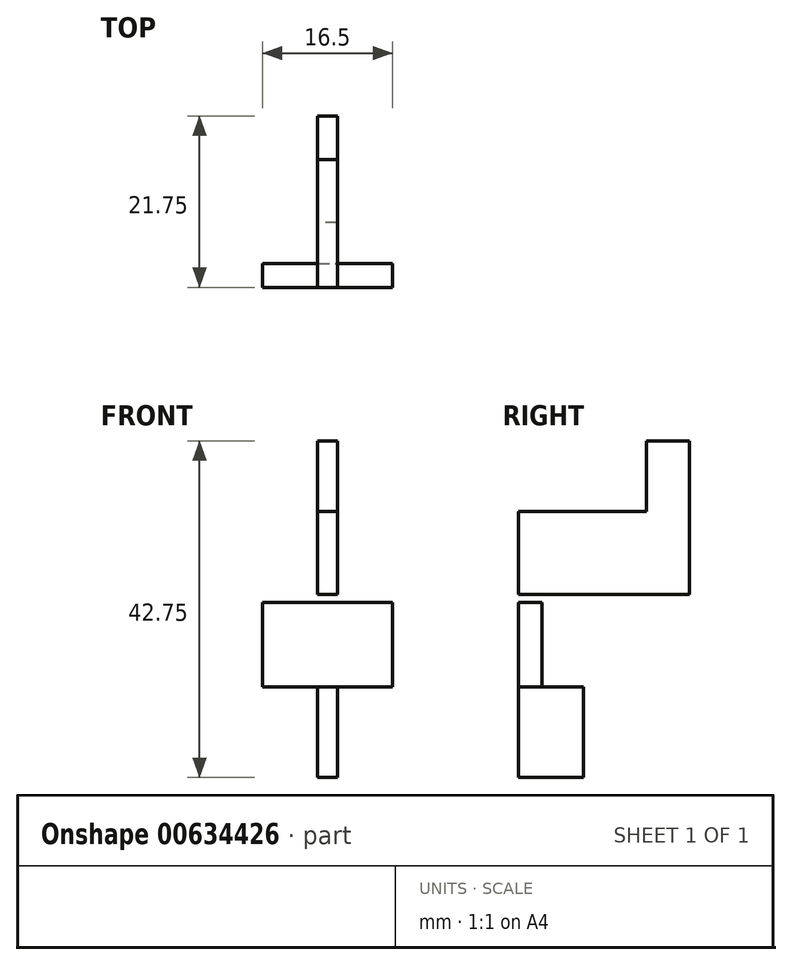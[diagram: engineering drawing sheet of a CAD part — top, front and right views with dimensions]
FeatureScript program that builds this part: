
annotation { "Feature Type Name" : "Feature", "Feature Type Description" : "" }
export const myFeature = defineFeature(function(context is Context, id is Id, definition is map)
    precondition{}
    {
        {
            var Q0;
            Q0=qCreatedBy(makeId("Right.planeOp"),FACE);
            var sketch = newSketch(context, id + "F0", { "sketchPlane" : qUnion([Q0])});
            skLineSegment(sketch, "E0.bottom", {"start": v(0, 0) * mm, "end": v(203.2, 0) * mm});
            skLineSegment(sketch, "E0.top", {"start": v(0, 5) * mm, "end": v(203.2, 5) * mm});
            skLineSegment(sketch, "E0.left", {"start": v(0, 0) * mm, "end": v(0, 5) * mm});
            skLineSegment(sketch, "E0.right", {"start": v(203.2, 0) * mm, "end": v(203.2, 5) * mm});
            skLineSegment(sketch, "E1.bottom", {"start": v(0, 0) * mm, "end": v(5, 0) * mm});
            skLineSegment(sketch, "E1.top", {"start": v(0, -95) * mm, "end": v(5, -95) * mm});
            skLineSegment(sketch, "E1.left", {"start": v(0, 0) * mm, "end": v(0, -95) * mm});
            skLineSegment(sketch, "E1.right", {"start": v(5, 0) * mm, "end": v(5, -95) * mm});
            skSolve(sketch);
        }
        {
            assignVariable(context, id + "F1", {"name" : "BracketThick", "anyValue" : 2.5 * mm});
        }
        {
            assignVariable(context, id + "F2", {"name" : "BracketNubThick", "anyValue" : 7 * mm});
        }
        {
            var Q0;
            Q0=qCreatedBy(makeId("Right.planeOp"),FACE);
            var sketch = newSketch(context, id + "F3", { "sketchPlane" : qUnion([Q0])});
            skLineSegment(sketch, "E2", {"start": v(0, -19.5) * mm, "end": v(0, -9) * mm});
            skLineSegment(sketch, "E3", {"start": v(0, -31.25) * mm, "end": v(0, -42.75) * mm});
            skLineSegment(sketch, "E4.MirrorCS", {"start": v(16.25, 0) * mm, "end": v(21.75, 0) * mm});
            skLineSegment(sketch, "E5.MirrorCS", {"start": v(8.25, -31.25) * mm, "end": v(0, -31.25) * mm});
            skLineSegment(sketch, "E6.MirrorCS", {"start": v(16.25, -9) * mm, "end": v(16.25, 0) * mm});
            skLineSegment(sketch, "E7.MirrorCS", {"start": v(0, -9) * mm, "end": v(16.25, -9) * mm});
            skLineSegment(sketch, "E8.MirrorCS", {"start": v(21.75, 0) * mm, "end": v(21.75, -19.5) * mm});
            skLineSegment(sketch, "E9.MirrorCS", {"start": v(0, -42.75) * mm, "end": v(8.25, -42.75) * mm});
            skLineSegment(sketch, "E10.MirrorCS", {"start": v(21.75, -19.5) * mm, "end": v(0, -19.5) * mm});
            skLineSegment(sketch, "E11.MirrorCS", {"start": v(8.25, -42.75) * mm, "end": v(8.25, -31.25) * mm});
            skLineSegment(sketch, "E12", {"start": v(3, -20.5) * mm, "end": v(3, -31.25) * mm});
            skLineSegment(sketch, "E13.MirrorCS", {"start": v(3, -31.25) * mm, "end": v(0, -31.25) * mm});
            skLineSegment(sketch, "E14.MirrorCS", {"start": v(0, -31.25) * mm, "end": v(0, -20.5) * mm});
            skLineSegment(sketch, "E15.MirrorCS", {"start": v(0, -20.5) * mm, "end": v(3, -20.5) * mm});
            skLineSegment(sketch, "E16.bottom", {"start": v(0, -19.5) * mm, "end": v(1, -19.5) * mm});
            skLineSegment(sketch, "E16.top", {"start": v(0, -20.5) * mm, "end": v(1, -20.5) * mm});
            skLineSegment(sketch, "E16.left", {"start": v(0, -19.5) * mm, "end": v(0, -20.5) * mm});
            skLineSegment(sketch, "E16.right", {"start": v(1, -19.5) * mm, "end": v(1, -20.5) * mm});
            skSolve(sketch);
        }
        {
            var Q0;
            Q0=makeQuery(id+"F3.imprint","IMPRINT",FACE,{"disambiguationData":[TD([[makeQuery(id+"F3.imprint","IMPRINT",EDGE,{"derivedFrom":sQuery(id+"F3.wireOp",EDGE,"E2")}),-1.0]])]});
            var Q1;
            Q1=makeQuery(id+"F3.imprint","IMPRINT",FACE,{"disambiguationData":[TD([[makeQuery(id+"F3.imprint","IMPRINT",EDGE,{"derivedFrom":sQuery(id+"F3.wireOp",EDGE,"E3")}),1.0]])]});
            extrude(context, id + "F4", {"entities" : qUnion([Q0, Q1]), "depth" : getVariable(context, 'BracketThick'), "offsetDistance" : 25 * mm});
        }
        {
            var Q0;
            Q0=makeQuery(id+"F3.imprint","IMPRINT",FACE,{"disambiguationData":[TD([[makeQuery(id+"F3.imprint","IMPRINT",EDGE,{"derivedFrom":sQuery(id+"F3.wireOp",EDGE,"E12")}),-1.0]])]});
            var Q1;
            Q1=makeQuery(id+"F3.imprint","IMPRINT",FACE,{"disambiguationData":[TD([[makeQuery(id+"F3.imprint","IMPRINT",EDGE,{"derivedFrom":sQuery(id+"F3.wireOp",EDGE,"E16.bottom")}),-1.0]])]});
            extrude(context, id + "F5", {"entities" : qUnion([Q0, Q1]), "oppositeDirection" : true, "depth" : getVariable(context, 'BracketNubThick'), "offsetDistance" : 25 * mm, "hasSecondDirection" : true, "secondDirectionOppositeDirection" : false, "secondDirectionDepth" : getVariable(context, 'BracketThick') + getVariable(context, 'BracketNubThick')});
        }
    });
